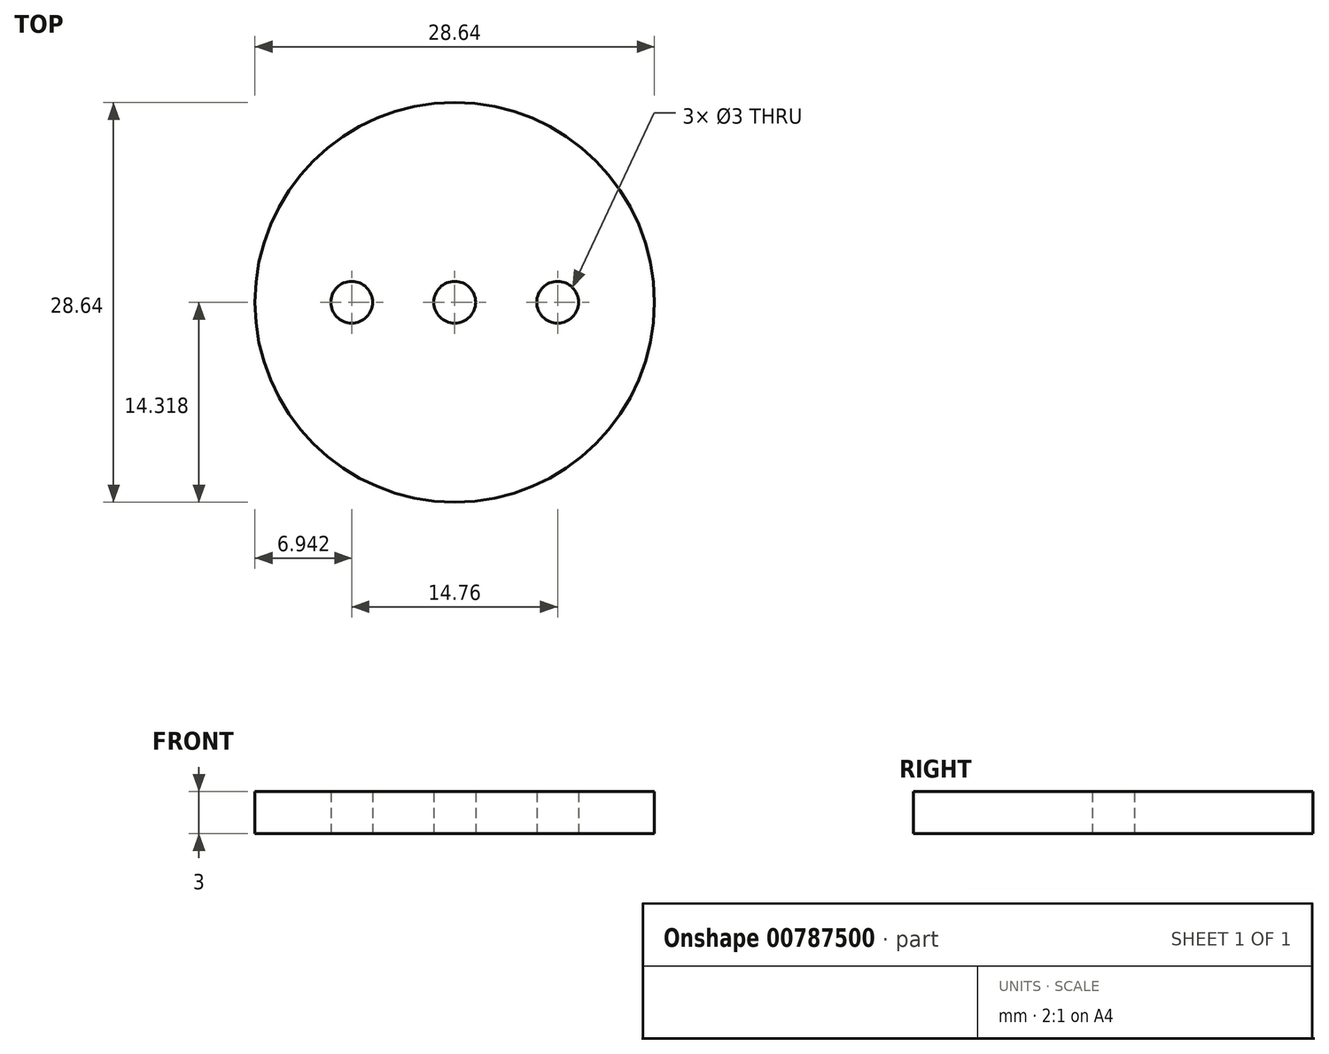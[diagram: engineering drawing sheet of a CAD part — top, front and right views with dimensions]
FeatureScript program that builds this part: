
annotation { "Feature Type Name" : "Feature", "Feature Type Description" : "" }
export const myFeature = defineFeature(function(context is Context, id is Id, definition is map)
    precondition{}
    {
        {
            var Q0;
            Q0=qCreatedBy(makeId("Top.planeOp"),FACE);
            var sketch = newSketch(context, id + "F0", { "sketchPlane" : qUnion([Q0])});
            skCircle(sketch, "E0", {"center": v(1.2, -1.2) * mm, "radius": 1.5 * mm});
            skCircle(sketch, "E1", {"center": v(8.58, -1.2) * mm, "radius": 1.5 * mm});
            skCircle(sketch, "E2", {"center": v(-6.18, -1.2) * mm, "radius": 1.5 * mm});
            skCircle(sketch, "E3", {"center": v(1.2, -1.2) * mm, "radius": 14.32 * mm});
            skSolve(sketch);
        }
        {
            var Q0;
            Q0=makeQuery(id+"F0.imprint","IMPRINT",FACE,{"disambiguationData":[TD([[makeQuery(id+"F0.imprint","IMPRINT",EDGE,{"derivedFrom":sQuery(id+"F0.wireOp",EDGE,"E0")}),-1.0]])]});
            extrude(context, id + "F1", {"entities" : qUnion([Q0]), "depth" : 3 * mm, "offsetDistance" : 25.4 * mm});
        }
    });
